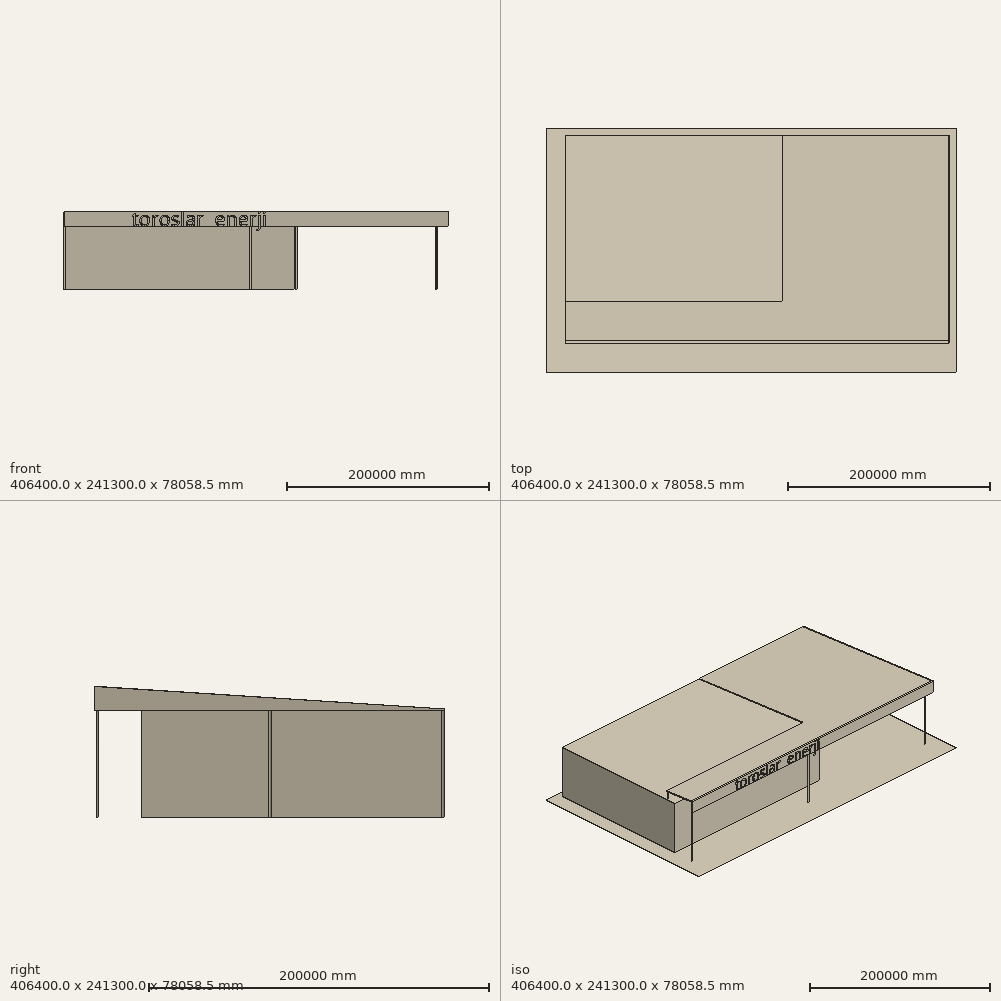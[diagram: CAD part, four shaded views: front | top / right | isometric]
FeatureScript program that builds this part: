
annotation { "Feature Type Name" : "Feature", "Feature Type Description" : "" }
export const myFeature = defineFeature(function(context is Context, id is Id, definition is map)
    precondition{}
    {
        {
            var Q0;
            Q0=qCreatedBy(makeId("Top.planeOp"),FACE);
            var sketch = newSketch(context, id + "F0", { "sketchPlane" : qUnion([Q0])});
            skLineSegment(sketch, "E0.bottom", {"start": v(0, 0) * mm, "end": v(406400, 0) * mm});
            skLineSegment(sketch, "E0.top", {"start": v(0, 241300) * mm, "end": v(406400, 241300) * mm});
            skLineSegment(sketch, "E0.left", {"start": v(0, 0) * mm, "end": v(0, 241300) * mm});
            skLineSegment(sketch, "E0.right", {"start": v(406400, 0) * mm, "end": v(406400, 241300) * mm});
            skLineSegment(sketch, "E1.bottom", {"start": v(18386.1, 234609.07) * mm, "end": v(246986.1, 234609.07) * mm});
            skLineSegment(sketch, "E1.top", {"start": v(18386.1, 56809.07) * mm, "end": v(246986.1, 56809.07) * mm});
            skLineSegment(sketch, "E1.left", {"start": v(18386.1, 234609.07) * mm, "end": v(18386.1, 56809.07) * mm});
            skLineSegment(sketch, "E1.right", {"start": v(246986.1, 234609.07) * mm, "end": v(246986.1, 56809.07) * mm});
            skSolve(sketch);
        }
        {
            var Q0;
            Q0=makeQuery(id+"F0.imprint","IMPRINT",FACE,{"disambiguationData":[TD([[makeQuery(id+"F0.imprint","IMPRINT",EDGE,{"derivedFrom":sQuery(id+"F0.wireOp",EDGE,"E1.bottom")}),-1.0]])]});
            extrude(context, id + "F1", {"entities" : qUnion([Q0]), "depth" : 63500 * mm, "offsetDistance" : 25.4 * mm});
        }
        {
            var Q0;
            Q0=makeQuery(id+"F0.imprint","IMPRINT",FACE,{"disambiguationData":[TD([[makeQuery(id+"F0.imprint","IMPRINT",EDGE,{"derivedFrom":sQuery(id+"F0.wireOp",EDGE,"E0.bottom")}),1.0]])]});
            extrude(context, id + "F2", {"entities" : qUnion([Q0]), "operationType" : NewBodyOperationType.ADD, "oppositeDirection" : true, "depth" : 25.4 * mm, "offsetDistance" : 25.4 * mm});
        }
        {
            var Q0;
            Q0=makeQuery(id+"F0.imprint","IMPRINT",FACE,{"disambiguationData":[TD([[makeQuery(id+"F0.imprint","IMPRINT",EDGE,{"derivedFrom":sQuery(id+"F0.wireOp",EDGE,"E0.bottom")}),1.0]])]});
            var sketch = newSketch(context, id + "F3", { "sketchPlane" : qUnion([Q0])});
            skCircle(sketch, "E2", {"center": v(19092.56, 30608.97) * mm, "radius": 800.1 * mm});
            skCircle(sketch, "E3.1.0.0", {"center": v(203242.56, 30608.97) * mm, "radius": 800.1 * mm});
            skCircle(sketch, "E3.2.0.0", {"center": v(387392.56, 30608.97) * mm, "radius": 800.1 * mm});
            skLineSegment(sketch, "E3.direction1", {"start": v(19092.56, 30608.97) * mm, "end": v(203242.56, 30608.97) * mm, "construction": true});
            skCircle(sketch, "E4.0.1.0", {"center": v(387392.56, 132208.97) * mm, "radius": 800.1 * mm});
            skCircle(sketch, "E4.0.2.0", {"center": v(387392.56, 233808.97) * mm, "radius": 800.1 * mm});
            skCircle(sketch, "E4.1.0.0", {"center": v(387417.96, 30608.97) * mm, "radius": 800.1 * mm});
            skCircle(sketch, "E4.1.1.0", {"center": v(387417.96, 132208.97) * mm, "radius": 800.1 * mm});
            skCircle(sketch, "E4.1.2.0", {"center": v(387417.96, 233808.97) * mm, "radius": 800.1 * mm});
            skCircle(sketch, "E4.2.0.0", {"center": v(387443.36, 30608.97) * mm, "radius": 800.1 * mm});
            skCircle(sketch, "E4.2.1.0", {"center": v(387443.36, 132208.97) * mm, "radius": 800.1 * mm});
            skCircle(sketch, "E4.2.2.0", {"center": v(387443.36, 233808.97) * mm, "radius": 800.1 * mm});
            skLineSegment(sketch, "E4.direction1", {"start": v(387392.56, 30608.97) * mm, "end": v(387417.96, 30608.97) * mm, "construction": true});
            skLineSegment(sketch, "E4.direction2", {"start": v(387392.56, 30608.97) * mm, "end": v(387392.56, 132208.97) * mm, "construction": true});
            skLineSegment(sketch, "E5", {"start": v(318063.26, 218781.7) * mm, "end": v(318063.26, 166467.94) * mm});
            skCircle(sketch, "E6.MirrorC", {"center": v(248683.16, 233808.97) * mm, "radius": 800.1 * mm});
            skCircle(sketch, "E7.MirrorC", {"center": v(248683.16, 132208.97) * mm, "radius": 800.1 * mm});
            skSolve(sketch);
        }
        {
            var Q0;
            Q0 = qSketchRegion(id + "F3", true);
            extrude(context, id + "F4", {"entities" : qUnion([Q0]), "operationType" : NewBodyOperationType.ADD, "depth" : 76200 * mm, "offsetDistance" : 25.4 * mm});
        }
        {
            var Q0;
            Q0=makeQuery(id+"F1.opExtrude","SWEPT_FACE",FACE,{"disambiguationData":[OSD([sQuery(id+"F0.wireOp",EDGE,"E1.right")])]});
            var sketch = newSketch(context, id + "F5", { "sketchPlane" : qUnion([Q0])});
            skLineSegment(sketch, "E8", {"start": v(31517.64, 76235.49) * mm, "end": v(234609.07, 63500) * mm});
            skLineSegment(sketch, "E9", {"start": v(234609.07, 63500) * mm, "end": v(235857.32, 63500) * mm});
            skLineSegment(sketch, "E10", {"start": v(235857.32, 63500) * mm, "end": v(235857.32, 78869.3) * mm});
            skLineSegment(sketch, "E11", {"start": v(235857.32, 78869.3) * mm, "end": v(31517.64, 76235.49) * mm});
            skSolve(sketch);
        }
        {
            var Q0;
            Q0 = qSketchRegion(id + "F5", true);
            var Q1;
            Q1=sQuery(id+"F5.wireOp",EDGE,"E8");
            var Q2;
            Q2=sQuery(id+"F5.wireOp",EDGE,"E11");
            var Q3;
            Q3=sQuery(id+"F5.wireOp",EDGE,"E10");
            var Q4;
            Q4=sQuery(id+"F5.wireOp",EDGE,"E9");
            extrude(context, id + "F6", {"entities" : qUnion([Q0]), "operationType" : NewBodyOperationType.REMOVE, "surfaceEntities" : qUnion([Q1, Q2, Q3, Q4]), "depth" : 177800 * mm, "offsetDistance" : 25.4 * mm});
        }
        {
            var Q0;
            Q0=makeQuery(id+"F1.opExtrude","SWEPT_FACE",FACE,{"disambiguationData":[OSD([sQuery(id+"F0.wireOp",EDGE,"E1.right")])]});
            var sketch = newSketch(context, id + "F7", { "sketchPlane" : qUnion([Q0])});
            skLineSegment(sketch, "E12", {"start": v(234609.07, 63500) * mm, "end": v(31373.89, 76200.08) * mm});
            skLineSegment(sketch, "E13", {"start": v(31373.89, 76200.08) * mm, "end": v(29865.96, 76200.08) * mm});
            skLineSegment(sketch, "E14", {"start": v(29865.96, 76200.08) * mm, "end": v(29865.96, 77251.06) * mm});
            skLineSegment(sketch, "E15", {"start": v(29865.96, 77251.06) * mm, "end": v(31396.74, 77251.06) * mm});
            skLineSegment(sketch, "E16", {"start": v(31396.74, 77251.06) * mm, "end": v(234609.07, 64041.18) * mm});
            skLineSegment(sketch, "E17", {"start": v(234609.07, 64041.18) * mm, "end": v(234609.07, 63500) * mm});
            skSolve(sketch);
        }
        {
            var Q0;
            Q0 = qSketchRegion(id + "F7", true);
            extrude(context, id + "F8", {"entities" : qUnion([Q0]), "operationType" : NewBodyOperationType.ADD, "depth" : 152400 * mm, "offsetDistance" : 25.4 * mm, "hasSecondDirection" : true, "secondDirectionOppositeDirection" : true, "secondDirectionDepth" : 12700 * mm});
        }
        {
            var Q0;
            Q0=makeQuery(id+"F8.opExtrude","CAP_FACE",FACE,{"disambiguationData":[OSD([sQuery(id+"F7.wireOp",EDGE,"E12"),sQuery(id+"F7.wireOp",EDGE,"E13"),sQuery(id+"F7.wireOp",EDGE,"E14"),sQuery(id+"F7.wireOp",EDGE,"E15"),sQuery(id+"F7.wireOp",EDGE,"E16"),sQuery(id+"F7.wireOp",EDGE,"E17")])],"isStart":true});
            var sketch = newSketch(context, id + "F9", { "sketchPlane" : qUnion([Q0])});
            skLineSegment(sketch, "E18", {"start": v(-29865.96, 76200.08) * mm, "end": v(-29865.96, 77251.06) * mm});
            skLineSegment(sketch, "E19", {"start": v(-29865.96, 77251.06) * mm, "end": v(-31396.74, 77251.06) * mm});
            skLineSegment(sketch, "E20", {"start": v(-31396.74, 77251.06) * mm, "end": v(-69766.36, 74756.83) * mm});
            skLineSegment(sketch, "E21", {"start": v(-69766.36, 74756.83) * mm, "end": v(-69704.48, 73804.82) * mm});
            skLineSegment(sketch, "E22", {"start": v(-69704.48, 73804.82) * mm, "end": v(-31373.89, 76200.08) * mm});
            skLineSegment(sketch, "E23", {"start": v(-31373.89, 76200.08) * mm, "end": v(-29865.96, 76200.08) * mm});
            skSolve(sketch);
        }
        {
            var Q0;
            Q0 = qSketchRegion(id + "F9", true);
            extrude(context, id + "F10", {"entities" : qUnion([Q0]), "operationType" : NewBodyOperationType.ADD, "depth" : 215900 * mm, "offsetDistance" : 25.4 * mm});
        }
        {
            var Q0;
            Q0=makeQuery(id+"F1.opExtrude","CAP_FACE",FACE,{"disambiguationData":[OSD([sQuery(id+"F0.wireOp",EDGE,"E1.bottom"),sQuery(id+"F0.wireOp",EDGE,"E1.top"),sQuery(id+"F0.wireOp",EDGE,"E1.left"),sQuery(id+"F0.wireOp",EDGE,"E1.right")])],"isStart":false});
            var sketch = newSketch(context, id + "F11", { "sketchPlane" : qUnion([Q0])});
            skCircle(sketch, "E24", {"center": v(19642.54, 68824.73) * mm, "radius": 800.1 * mm});
            skCircle(sketch, "E25.1.0.0", {"center": v(88222.54, 68824.73) * mm, "radius": 800.1 * mm});
            skCircle(sketch, "E25.2.0.0", {"center": v(156802.54, 68824.73) * mm, "radius": 800.1 * mm});
            skCircle(sketch, "E25.3.0.0", {"center": v(225382.54, 68824.73) * mm, "radius": 800.1 * mm});
            skLineSegment(sketch, "E25.direction1", {"start": v(19642.54, 68824.73) * mm, "end": v(88222.54, 68824.73) * mm, "construction": true});
            skSolve(sketch);
        }
        {
            var Q0;
            Q0 = qSketchRegion(id + "F11", true);
            extrude(context, id + "F12", {"entities" : qUnion([Q0]), "endBound" : BoundingType.UP_TO_NEXT, "depth" : 25.4 * mm, "offsetDistance" : 25.4 * mm});
        }
        {
            var Q0;
            Q0=makeQuery(id+"F10.boolean.opBoolean","MERGE",FACE,{"derivedFrom":[makeQuery(id+"F8.opExtrude","SWEPT_FACE",FACE,{"disambiguationData":[OSD([sQuery(id+"F7.wireOp",EDGE,"E14")])]}),makeQuery(id+"F10.opExtrude","SWEPT_FACE",FACE,{"disambiguationData":[OSD([sQuery(id+"F9.wireOp",EDGE,"E18")])]})]});
            var sketch = newSketch(context, id + "F13", { "sketchPlane" : qUnion([Q0])});
            skLineSegment(sketch, "E26.bottom", {"start": v(18386.1, 77251.06) * mm, "end": v(399386.1, 77251.06) * mm});
            skLineSegment(sketch, "E26.top", {"start": v(18386.1, 63119.43) * mm, "end": v(399386.1, 63119.43) * mm});
            skLineSegment(sketch, "E26.left", {"start": v(18386.1, 77251.06) * mm, "end": v(18386.1, 63119.43) * mm});
            skLineSegment(sketch, "E26.right", {"start": v(399386.1, 77251.06) * mm, "end": v(399386.1, 63119.43) * mm});
            skSolve(sketch);
        }
        {
            var Q0;
            Q0 = qSketchRegion(id + "F13", true);
            extrude(context, id + "F14", {"entities" : qUnion([Q0]), "operationType" : NewBodyOperationType.ADD, "depth" : 1016 * mm, "offsetDistance" : 25.4 * mm});
        }
        {
            var Q0;
            Q0=makeQuery(id+"F14.opExtrude","CAP_FACE",FACE,{"disambiguationData":[OSD([sQuery(id+"F13.wireOp",EDGE,"E26.bottom"),sQuery(id+"F13.wireOp",EDGE,"E26.top"),sQuery(id+"F13.wireOp",EDGE,"E26.left"),sQuery(id+"F13.wireOp",EDGE,"E26.right")])],"isStart":false});
            var sketch = newSketch(context, id + "F15", { "sketchPlane" : qUnion([Q0])});
            skText(sketch, "E27", { "text": "toroslar  enerji", "fontName": "OpenSans-Regular.ttf"});
            const initialGuessF15  = {"E27": [85.53704, 63.11943, 1, 0, 14.13163]};
            skSetInitialGuess(sketch, initialGuessF15);
            skSolve(sketch);
        }
        {
            var Q0;
            Q0 = qSketchRegion(id + "F15", true);
            extrude(context, id + "F16", {"entities" : qUnion([Q0]), "operationType" : NewBodyOperationType.ADD, "depth" : 254 * mm, "offsetDistance" : 25.4 * mm});
        }
        {
            var Q0;
            {var subQ4=sQuery(id+"F0.wireOp",EDGE,"E1.right");var subQ10=sQuery(id+"F0.wireOp",EDGE,"E1.bottom");var subQ16=sQuery(id+"F0.wireOp",EDGE,"E0.right");var subQ19=sQuery(id+"F0.wireOp",EDGE,"E0.left");var subQ22=sQuery(id+"F0.wireOp",EDGE,"E0.top");var subQ26=sQuery(id+"F0.wireOp",EDGE,"E0.bottom");var subQ27=sQuery(id+"F0.wireOp",EDGE,"E1.top");var subQ28=sQuery(id+"F0.wireOp",EDGE,"E1.left");Q0=makeQuery(id+"F4.boolean.opBoolean","SPLIT",FACE,{"disambiguationData":[TD([makeQuery(id+"F2.opExtrude","SWEPT_FACE",FACE,{"disambiguationData":[OSD([subQ26])]})])],"derivedFrom":makeQuery(id+"F2.opExtrude","CAP_FACE",FACE,{"disambiguationData":[OSD([subQ26,subQ22,subQ19,subQ16,subQ10,subQ27,subQ28,subQ4])],"isStart":true})});}
            var sketch = newSketch(context, id + "F17", { "sketchPlane" : qUnion([Q0])});
            skLineSegment(sketch, "E28.bottom", {"start": v(0, 0) * mm, "end": v(406400, 0) * mm});
            skLineSegment(sketch, "E28.top", {"start": v(0, 241300) * mm, "end": v(406400, 241300) * mm});
            skLineSegment(sketch, "E28.left", {"start": v(0, 0) * mm, "end": v(0, 241300) * mm});
            skLineSegment(sketch, "E28.right", {"start": v(406400, 0) * mm, "end": v(406400, 241300) * mm});
            skSolve(sketch);
        }
        {
            var Q0;
            Q0 = qSketchRegion(id + "F17", true);
            extrude(context, id + "F18", {"entities" : qUnion([Q0]), "depth" : 25.4 * mm, "offsetDistance" : 25.4 * mm});
        }
        {
            var Q0;
            {var subQ18=sQuery(id+"F13.wireOp",EDGE,"E26.bottom");var subQ40=sQuery(id+"F13.wireOp",EDGE,"E26.right");var subQ45=sQuery(id+"F13.wireOp",EDGE,"E26.top");Q0=makeQuery(id+"F16.boolean.opBoolean","SPLIT",FACE,{"disambiguationData":[TD([makeQuery(id+"F14.opExtrude","SWEPT_FACE",FACE,{"disambiguationData":[OSD([subQ40])]})])],"derivedFrom":makeQuery(id+"F14.opExtrude","CAP_FACE",FACE,{"disambiguationData":[OSD([subQ18,subQ45,sQuery(id+"F13.wireOp",EDGE,"E26.left"),subQ40])],"isStart":false})});}
            var sketch = newSketch(context, id + "F19", { "sketchPlane" : qUnion([Q0])});
            skLineSegment(sketch, "E29.bottom", {"start": v(399386.1, 77251.06) * mm, "end": v(398653.23, 77251.06) * mm});
            skLineSegment(sketch, "E29.top", {"start": v(399386.1, 63119.43) * mm, "end": v(398653.23, 63119.43) * mm});
            skLineSegment(sketch, "E29.left", {"start": v(399386.1, 77251.06) * mm, "end": v(399386.1, 63119.43) * mm});
            skLineSegment(sketch, "E29.right", {"start": v(398653.23, 77251.06) * mm, "end": v(398653.23, 63119.43) * mm});
            skSolve(sketch);
        }
        {
            var Q0;
            Q0 = qSketchRegion(id + "F19", true);
            extrude(context, id + "F20", {"entities" : qUnion([Q0]), "operationType" : NewBodyOperationType.ADD, "oppositeDirection" : true, "depth" : 205740 * mm, "offsetDistance" : 25.4 * mm});
        }
        {
            var Q0;
            Q0=makeQuery(id+"F20.boolean.opBoolean","MERGE",FACE,{"derivedFrom":[makeQuery(id+"F14.boolean.opBoolean","MERGE",FACE,{"derivedFrom":[makeQuery(id+"F8.opExtrude","CAP_FACE",FACE,{"disambiguationData":[OSD([sQuery(id+"F7.wireOp",EDGE,"E12"),sQuery(id+"F7.wireOp",EDGE,"E13"),sQuery(id+"F7.wireOp",EDGE,"E14"),sQuery(id+"F7.wireOp",EDGE,"E15"),sQuery(id+"F7.wireOp",EDGE,"E16"),sQuery(id+"F7.wireOp",EDGE,"E17")])],"isStart":false}),makeQuery(id+"F14.opExtrude","SWEPT_FACE",FACE,{"disambiguationData":[OSD([sQuery(id+"F13.wireOp",EDGE,"E26.right")])]})]}),makeQuery(id+"F20.opExtrude","SWEPT_FACE",FACE,{"disambiguationData":[OSD([sQuery(id+"F19.wireOp",EDGE,"E29.left")])]})]});
            var sketch = newSketch(context, id + "F21", { "sketchPlane" : qUnion([Q0])});
            skLineSegment(sketch, "E30", {"start": v(234609.07, 64041.18) * mm, "end": v(28849.96, 77251.06) * mm});
            skLineSegment(sketch, "E31", {"start": v(28849.96, 77251.06) * mm, "end": v(28849.96, 79047.65) * mm});
            skLineSegment(sketch, "E32", {"start": v(28849.96, 79047.65) * mm, "end": v(236006.53, 79047.65) * mm});
            skLineSegment(sketch, "E33", {"start": v(236006.53, 79047.65) * mm, "end": v(236006.53, 64041.18) * mm});
            skLineSegment(sketch, "E34", {"start": v(236006.53, 64041.18) * mm, "end": v(234609.07, 64041.18) * mm});
            skSolve(sketch);
        }
        {
            var Q0;
            Q0 = qSketchRegion(id + "F21", true);
            extrude(context, id + "F22", {"entities" : qUnion([Q0]), "operationType" : NewBodyOperationType.REMOVE, "oppositeDirection" : true, "depth" : 1016 * mm, "offsetDistance" : 25.4 * mm});
        }
    });
